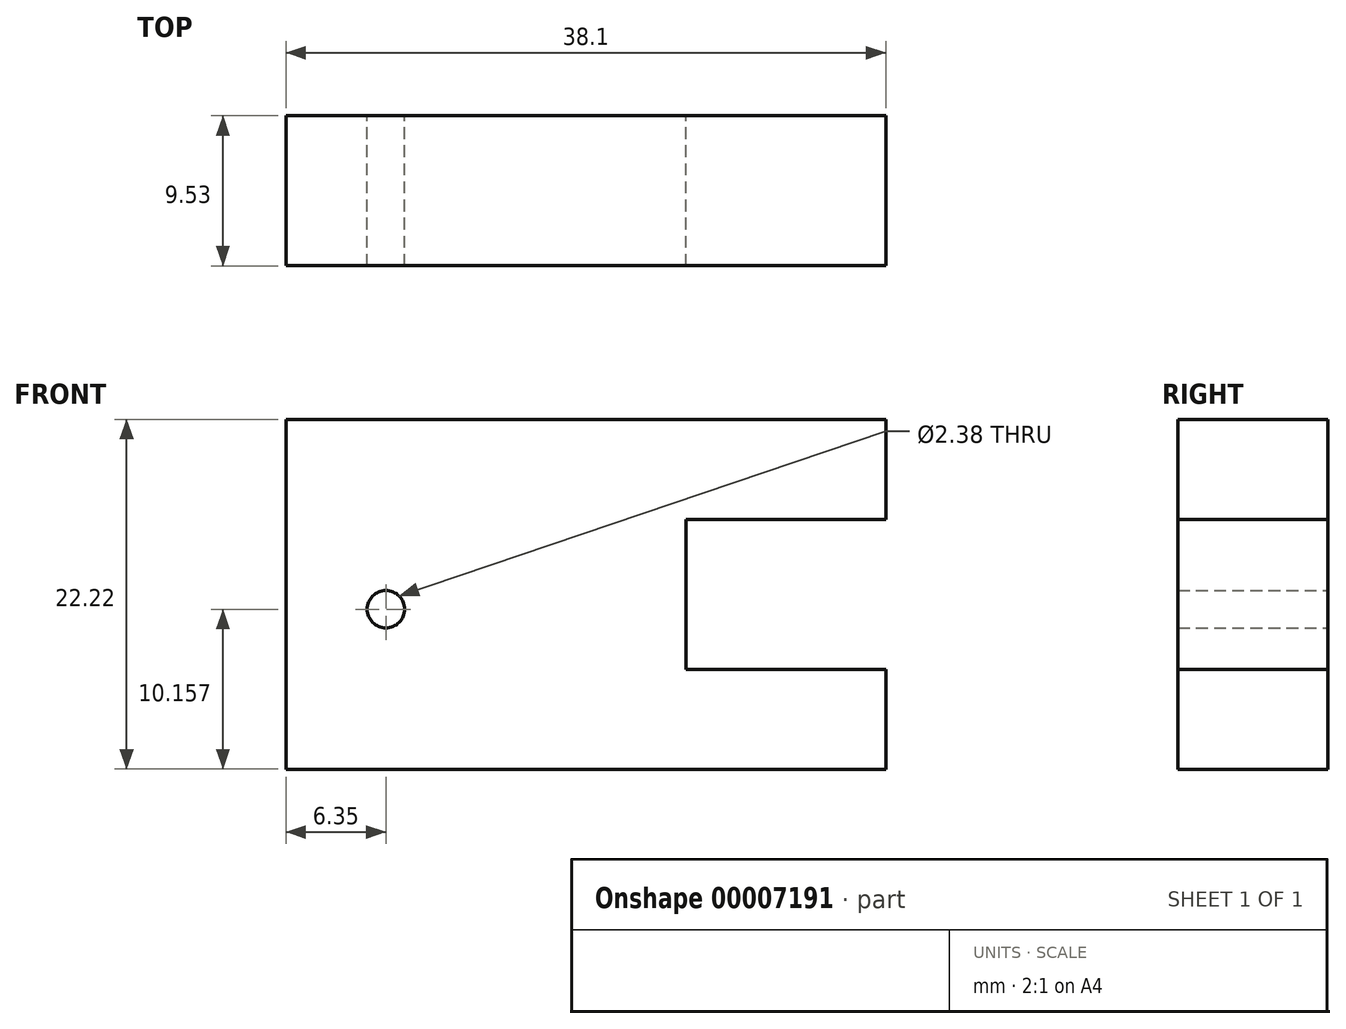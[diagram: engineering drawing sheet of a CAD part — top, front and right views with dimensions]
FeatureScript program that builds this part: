
annotation { "Feature Type Name" : "Feature", "Feature Type Description" : "" }
export const myFeature = defineFeature(function(context is Context, id is Id, definition is map)
    precondition{}
    {
        {
            var Q0;
            Q0=qCreatedBy(makeId("Front.planeOp"),FACE);
            var sketch = newSketch(context, id + "F0", { "sketchPlane" : qUnion([Q0])});
            skLineSegment(sketch, "E0", {"start": v(-25.4, -11.11) * mm, "end": v(-25.4, 11.11) * mm});
            skLineSegment(sketch, "E1", {"start": v(-25.4, 11.11) * mm, "end": v(12.7, 11.11) * mm});
            skLineSegment(sketch, "E2", {"start": v(12.7, 11.11) * mm, "end": v(12.7, 4.76) * mm});
            skLineSegment(sketch, "E3", {"start": v(12.7, 4.76) * mm, "end": v(0, 4.76) * mm});
            skLineSegment(sketch, "E4", {"start": v(0, 4.76) * mm, "end": v(0, -4.76) * mm});
            skLineSegment(sketch, "E5", {"start": v(0, -4.76) * mm, "end": v(12.7, -4.76) * mm});
            skLineSegment(sketch, "E6", {"start": v(12.7, -4.76) * mm, "end": v(12.7, -11.11) * mm});
            skLineSegment(sketch, "E7", {"start": v(12.7, -11.11) * mm, "end": v(-25.4, -11.11) * mm});
            skLineSegment(sketch, "E8", {"start": v(-29.92, 0) * mm, "end": v(27.74, 0) * mm});
            skCircle(sketch, "E9", {"center": v(-19.05, -0.95) * mm, "radius": 1.2 * mm});
            skSolve(sketch);
        }
        {
            var Q0;
            {var subQ6=sQuery(id+"F0.wireOp",EDGE,"E1");Q0=makeQuery(id+"F0.imprint","IMPRINT",FACE,{"disambiguationData":[TD([[makeQuery(id+"F0.imprint","IMPRINT",EDGE,{"derivedFrom":subQ6}),-1.0]])]});}
            var Q1;
            {var subQ6=sQuery(id+"F0.wireOp",EDGE,"E5");Q1=makeQuery(id+"F0.imprint","IMPRINT",FACE,{"disambiguationData":[TD([[makeQuery(id+"F0.imprint","IMPRINT",EDGE,{"derivedFrom":subQ6}),-1.0]])]});}
            extrude(context, id + "F1", {"entities" : qUnion([Q0, Q1]), "depth" : 9.52 * mm});
        }
    });
